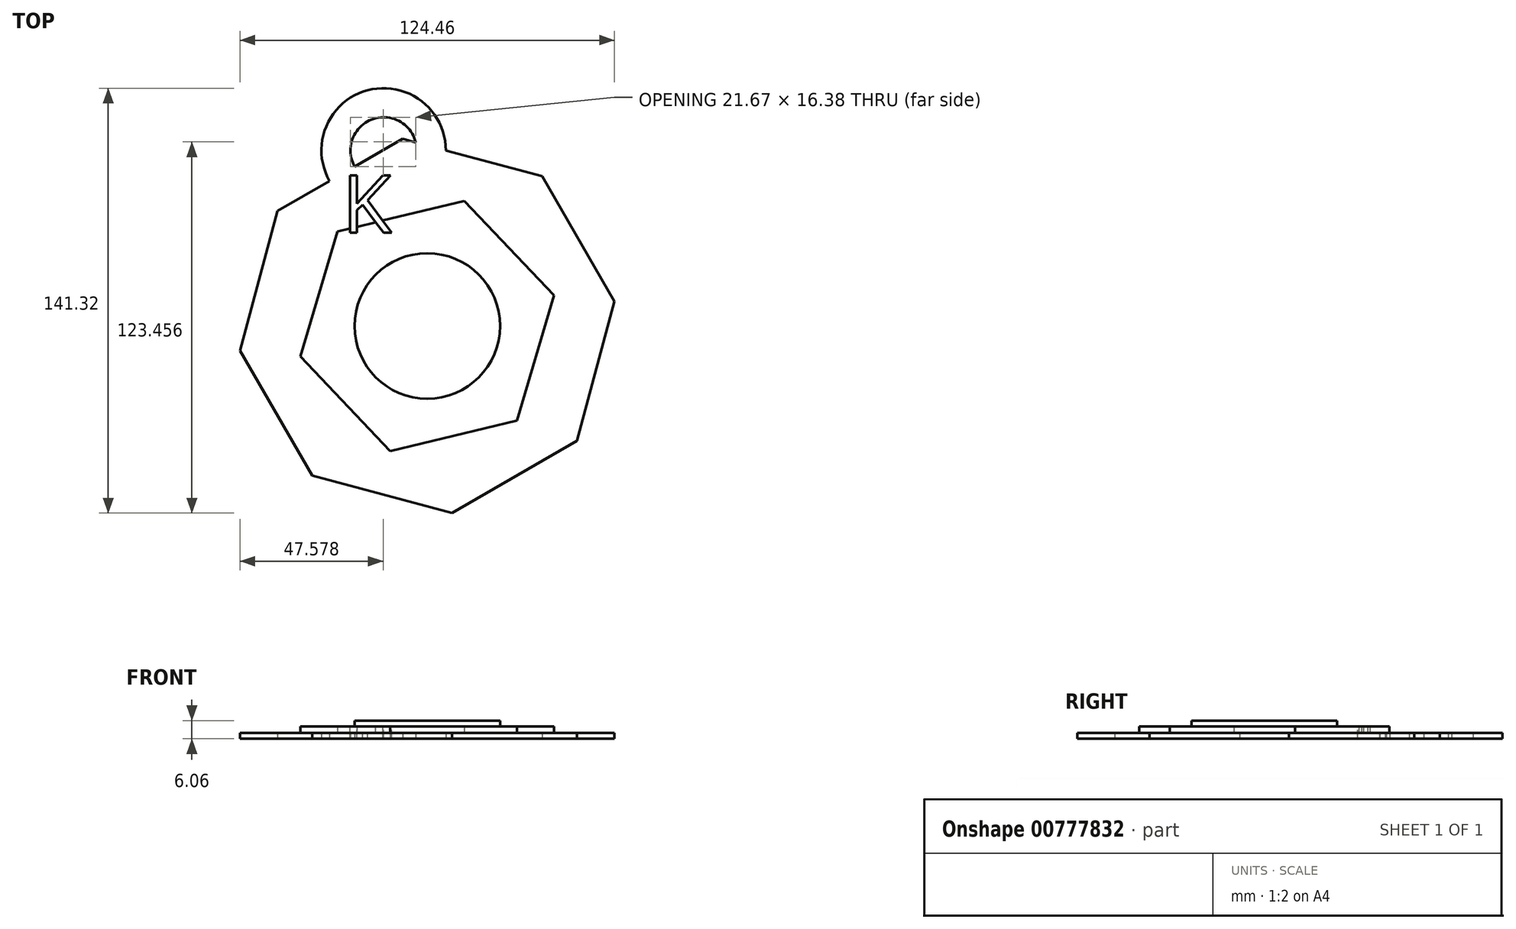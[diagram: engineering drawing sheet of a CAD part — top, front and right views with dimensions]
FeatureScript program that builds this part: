
annotation { "Feature Type Name" : "Feature", "Feature Type Description" : "" }
export const myFeature = defineFeature(function(context is Context, id is Id, definition is map)
    precondition{}
    {
        {
            var Q0;
            Q0=qCreatedBy(makeId("Top.planeOp"),FACE);
            var sketch = newSketch(context, id + "F0", { "sketchPlane" : qUnion([Q0])});
            skCircle(sketch, "E0.cCircle", {"center": v(0, 0) * mm, "radius": 57.99 * mm, "construction": true});
            skLineSegment(sketch, "E0.0", {"start": v(49.8, -38.2) * mm, "end": v(8.2, -62.23) * mm});
            skLineSegment(sketch, "E0.1", {"start": v(8.2, -62.23) * mm, "end": v(-38.2, -49.8) * mm});
            skLineSegment(sketch, "E0.2", {"start": v(-38.2, -49.8) * mm, "end": v(-62.23, -8.2) * mm});
            skLineSegment(sketch, "E0.3", {"start": v(-62.23, -8.2) * mm, "end": v(-49.8, 38.2) * mm});
            skLineSegment(sketch, "E0.4", {"start": v(-49.8, 38.2) * mm, "end": v(-8.2, 62.23) * mm});
            skLineSegment(sketch, "E0.5", {"start": v(-8.2, 62.23) * mm, "end": v(38.2, 49.8) * mm});
            skLineSegment(sketch, "E0.6", {"start": v(38.2, 49.8) * mm, "end": v(62.23, 8.2) * mm});
            skLineSegment(sketch, "E0.7", {"start": v(62.23, 8.2) * mm, "end": v(49.8, -38.2) * mm});
            skPoint(sketch, "E0.0.midPoint", {"position": v(29, -50.22) * mm});
            skSolve(sketch);
        }
        {
            var Q0;
            Q0=makeQuery(id+"F0.imprint","IMPRINT",FACE,{"disambiguationData":[TD([[makeQuery(id+"F0.imprint","IMPRINT",EDGE,{"derivedFrom":sQuery(id+"F0.wireOp",EDGE,"E0.0")}),-1.0]])]});
            extrude(context, id + "F1", {"entities" : qUnion([Q0]), "depth" : 2 * mm, "offsetDistance" : 25.4 * mm});
        }
        {
            var Q0;
            Q0=makeQuery(id+"F1.opExtrude","CAP_FACE",FACE,{"disambiguationData":[OSD([sQuery(id+"F0.wireOp",EDGE,"E0.0"),sQuery(id+"F0.wireOp",EDGE,"E0.1"),sQuery(id+"F0.wireOp",EDGE,"E0.2"),sQuery(id+"F0.wireOp",EDGE,"E0.3"),sQuery(id+"F0.wireOp",EDGE,"E0.4"),sQuery(id+"F0.wireOp",EDGE,"E0.5"),sQuery(id+"F0.wireOp",EDGE,"E0.6"),sQuery(id+"F0.wireOp",EDGE,"E0.7")])],"isStart":true});
            var sketch = newSketch(context, id + "F2", { "sketchPlane" : qUnion([Q0])});
            skCircle(sketch, "E1.cCircle", {"center": v(0, 0) * mm, "radius": 37.55 * mm, "construction": true});
            skLineSegment(sketch, "E1.0", {"start": v(-12.29, 41.59) * mm, "end": v(29.87, 31.43) * mm});
            skLineSegment(sketch, "E1.1", {"start": v(29.87, 31.43) * mm, "end": v(42.16, -10.15) * mm});
            skLineSegment(sketch, "E1.2", {"start": v(42.16, -10.15) * mm, "end": v(12.29, -41.59) * mm});
            skLineSegment(sketch, "E1.3", {"start": v(12.29, -41.59) * mm, "end": v(-29.87, -31.43) * mm});
            skLineSegment(sketch, "E1.4", {"start": v(-29.87, -31.43) * mm, "end": v(-42.16, 10.15) * mm});
            skLineSegment(sketch, "E1.5", {"start": v(-42.16, 10.15) * mm, "end": v(-12.29, 41.59) * mm});
            skPoint(sketch, "E1.0.midPoint", {"position": v(8.8, 36.51) * mm});
            skSolve(sketch);
        }
        {
            var Q0;
            Q0=makeQuery(id+"F2.imprint","IMPRINT",FACE,{"disambiguationData":[TD([[makeQuery(id+"F2.imprint","IMPRINT",EDGE,{"derivedFrom":sQuery(id+"F2.wireOp",EDGE,"E1.0")}),-1.0]])]});
            extrude(context, id + "F3", {"entities" : qUnion([Q0]), "operationType" : NewBodyOperationType.ADD, "oppositeDirection" : true, "depth" : 4.06 * mm, "offsetDistance" : 25.4 * mm});
        }
        {
            var Q0;
            Q0=makeQuery(id+"F3.opExtrude","CAP_FACE",FACE,{"disambiguationData":[OSD([sQuery(id+"F2.wireOp",EDGE,"E1.0"),sQuery(id+"F2.wireOp",EDGE,"E1.1"),sQuery(id+"F2.wireOp",EDGE,"E1.2"),sQuery(id+"F2.wireOp",EDGE,"E1.3"),sQuery(id+"F2.wireOp",EDGE,"E1.4"),sQuery(id+"F2.wireOp",EDGE,"E1.5")])],"isStart":false});
            var sketch = newSketch(context, id + "F4", { "sketchPlane" : qUnion([Q0])});
            skCircle(sketch, "E2", {"center": v(0, 0) * mm, "radius": 24.18 * mm});
            skSolve(sketch);
        }
        {
            var Q0;
            Q0 = qSketchRegion(id + "F4", true);
            extrude(context, id + "F5", {"entities" : qUnion([Q0]), "operationType" : NewBodyOperationType.ADD, "depth" : 2 * mm, "offsetDistance" : 25.4 * mm});
        }
        {
            var Q0;
            Q0=qCreatedBy(makeId("Top.planeOp"),FACE);
            var sketch = newSketch(context, id + "F6", { "sketchPlane" : qUnion([Q0])});
            skCircle(sketch, "E3", {"center": v(-14.51, 58.42) * mm, "radius": 20.67 * mm});
            skCircle(sketch, "E4", {"center": v(-14.51, 58.42) * mm, "radius": 11.01 * mm});
            skSolve(sketch);
        }
        {
            var Q0;
            Q0=makeQuery(id+"F6.imprint","IMPRINT",FACE,{"disambiguationData":[TD([[makeQuery(id+"F6.imprint","IMPRINT",EDGE,{"derivedFrom":sQuery(id+"F6.wireOp",EDGE,"E3")}),1.0]])]});
            extrude(context, id + "F7", {"entities" : qUnion([Q0]), "operationType" : NewBodyOperationType.ADD, "depth" : 2 * mm, "offsetDistance" : 25.4 * mm});
        }
        {
            var Q0;
            Q0=makeQuery(id+"F5.opExtrude","CAP_FACE",FACE,{"disambiguationData":[OSD([sQuery(id+"F4.wireOp",EDGE,"E2")])],"isStart":false});
            var sketch = newSketch(context, id + "F8", { "sketchPlane" : qUnion([Q0])});
            skText(sketch, "E5", { "text": "K", "fontName": "OpenSans-Regular.ttf"});
            const initialGuessF8  = {"E5": [-0.02829, 0.03102, 1, 0, 0.01927]};
            skSetInitialGuess(sketch, initialGuessF8);
            skSolve(sketch);
        }
        {
            var Q0;
            Q0 = qSketchRegion(id + "F8", true);
            extrude(context, id + "F9", {"entities" : qUnion([Q0]), "operationType" : NewBodyOperationType.REMOVE, "oppositeDirection" : true, "depth" : 25.4 * mm, "offsetDistance" : 25.4 * mm});
        }
    });
